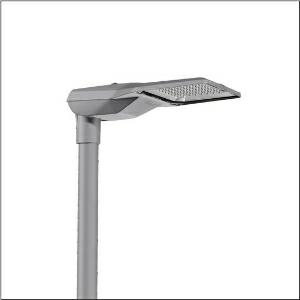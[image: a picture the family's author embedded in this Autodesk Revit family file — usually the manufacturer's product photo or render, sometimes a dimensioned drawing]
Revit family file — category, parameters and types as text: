
# Revit family: streetlight_sl_21_midi___p0_5a_5xe3v33s08lb_b536
name_source: partatom
category: Lighting Fixtures
units: mm (PartAtom-declared; Revit-internal decimal feet)

## family parameters
Cut with Voids When Loaded = No
Host = Face
Light Source = No
Part Type = Normal
Room Calculation Point = No
Round Connector Dimension = Use Diameter
Shared = No

## types (1)
- --- (1 x LED, 14100 lm, 99.6 W, 3000K)
    Apparent Load = 100 VA
    CIE Flux Codes = 37 73 96 100 100
    Color Rendering = 70
    Color Temperature = 3000K
    Default Elevation = 1800 mm
    Description = Streetlight SL 21 midi, mast luminaire, primary light control with lens, of PMMA, primary optical cover: cover, of toughened safety glass, transparent, light distribution: P0.5a, light emission: direct distribution, primary light characteristic: asymmetric, installation type: post-top, side-entry, LED, High Power LED, rated luminous flux: 14.100lm, luminous efficacy: 142lm/W, light colour: 730, colour temperature: 3000K, control gear: D4i, control: pre-setting: logarithmic dimming characteristic, flexible luminous flux parameterisation, time-dependent luminous flux control, constant luminous flux control, overheat protection, mains connection: 230..240V, AC, 50/60Hz, start of lifetime: 100W, end of service life: 102W, reduction: 46W, luminaire housing, of diecast aluminium, powder-coated, Siteco® metallic grey (DB 702S), corrosivity category C5 mid according to DIN EN ISO 12944, multi-level sealing system, sealing non-destructively replaceable, inclination adjustable: 0°, 5°, 10°, 15°, please order mast flange separately, length: 644mm, width: 335mm, height: 110mm, mast flange for spigot size: 42mm (side-entry): 5XC10008XM4, 60/48mm (side-entry/post-top): 5XC10108XM2, 76/60mm (side-entry/post-top): 5XC10108XM1, mounting height: 4..8m, Smart Interface above, protection rating (complete): IP66, insulation class (complete): insulation class II (safety insulation), certification: CE, ENEC, ENEC+, VDE, impact resistance: IK10, permissible operating ambient temperature for outdoor applications: -40..+50°C, standard-compliant lighting for roads and squares, packaging unit: 1 piece

Light Distribution: P0.5a
    Height = 111 mm
    Lamp = 1 x LED
    Lamp Light Flux = 14100 lm
    Lamp Power = 99.6 W
    Lamp count = 1
    Length = 644 mm
    Luminous efficacy = 142 lm/W
    Manufacturer = Siteco
    ModVariant = No
    Model = 5XE3V33S08LB
    Number of Poles = 1
    OnlyDefault = Yes
    Power Factor = 1
    Product Name = Streetlight SL 21 midi | P0.5a
    Product group = mast luminaire | pylon top
    ProductGroupID = 6100
    Protection Class = Protection class II
    Protection Degree = IP 66
    RLX_Detail_Level = 1
    RLX_Emergency_Light_Flux = 0 lm
    RLX_Emergency_Type = 0
    RLX_Emergency_Type_DB = No
    RlxData = <blob elided: 26369 chars, md5=21ab7c55>
    Socket = socket
    Standby Power = 0 W
    System Light Flux = 14100 lm
    System Power = 100 W
    Type Comments = factory setting: luminous flux: 100 % | dim-lin: 254 | 1020 mA
    Type Image = l_1004302.jpg
    URL = http://relux.com
    VarID = @adj_033091
    Voltage = 0 V
    Weight = 0.00 kg
    Width = 336 mm

## geometry (parser evidence)
native form markers: Blend x4, Sweep x12
no freeform markers — native parametric forms only
